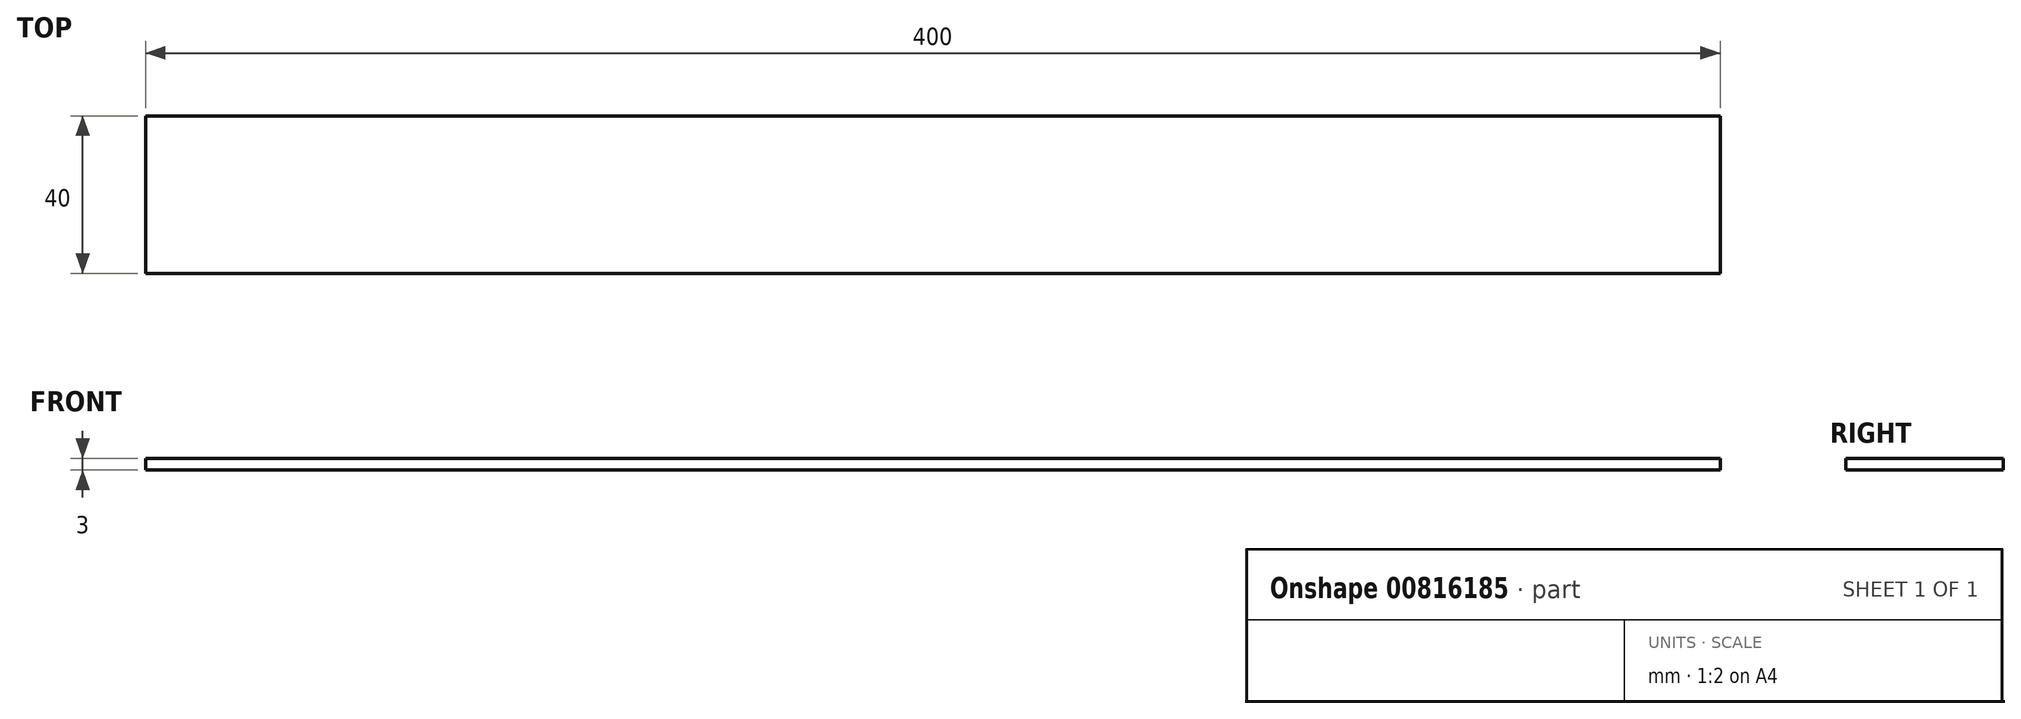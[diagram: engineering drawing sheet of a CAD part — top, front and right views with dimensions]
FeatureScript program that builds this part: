
annotation { "Feature Type Name" : "Feature", "Feature Type Description" : "" }
export const myFeature = defineFeature(function(context is Context, id is Id, definition is map)
    precondition{}
    {
        {
            var Q0;
            Q0=qCreatedBy(makeId("Top.planeOp"),FACE);
            var sketch = newSketch(context, id + "F0", { "sketchPlane" : qUnion([Q0])});
            skLineSegment(sketch, "E0.bottom", {"start": v(200, 20) * mm, "end": v(-200, 20) * mm});
            skLineSegment(sketch, "E0.top", {"start": v(200, -20) * mm, "end": v(-200, -20) * mm});
            skLineSegment(sketch, "E0.left", {"start": v(200, 20) * mm, "end": v(200, -20) * mm});
            skLineSegment(sketch, "E0.right", {"start": v(-200, 20) * mm, "end": v(-200, -20) * mm});
            skPoint(sketch, "E0.middle", {"position": v(0, 0) * mm});
            skSolve(sketch);
        }
        {
            var Q0;
            Q0=makeQuery(id+"F0.imprint","IMPRINT",FACE,{"disambiguationData":[TD([[makeQuery(id+"F0.imprint","IMPRINT",EDGE,{"derivedFrom":sQuery(id+"F0.wireOp",EDGE,"E0.bottom")}),1.0]])]});
            extrude(context, id + "F1", {"entities" : qUnion([Q0]), "depth" : 3 * mm, "offsetDistance" : 25 * mm});
        }
    });
